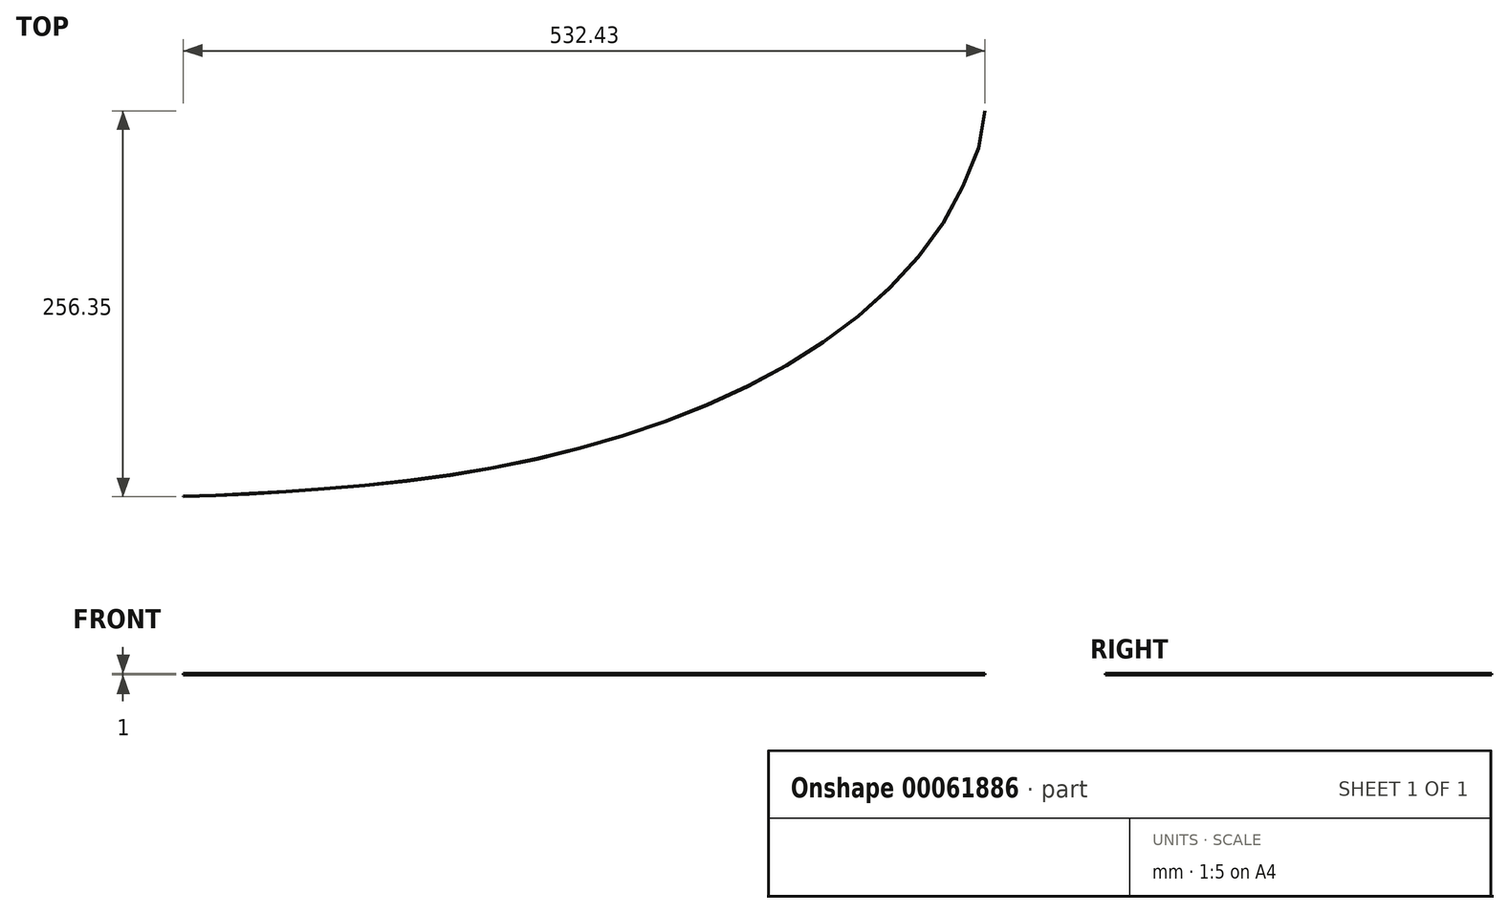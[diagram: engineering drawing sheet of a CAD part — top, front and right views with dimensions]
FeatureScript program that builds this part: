
annotation { "Feature Type Name" : "Feature", "Feature Type Description" : "" }
export const myFeature = defineFeature(function(context is Context, id is Id, definition is map)
    precondition{}
    {
        {
            var Q0;
            Q0=qCreatedBy(makeId("Top.planeOp"),FACE);
            var sketch = newSketch(context, id + "F0", { "sketchPlane" : qUnion([Q0])});
            skPoint(sketch, "E0", {"position": v(15.35, 547.94) * mm});
            skPoint(sketch, "E1", {"position": v(32.44, 548.38) * mm});
            skPoint(sketch, "E2", {"position": v(51.35, 549.15) * mm});
            skPoint(sketch, "E3", {"position": v(72.4, 550.32) * mm});
            skPoint(sketch, "E4", {"position": v(96.02, 551.9) * mm});
            skPoint(sketch, "E5", {"position": v(122.25, 553.98) * mm});
            skPoint(sketch, "E6", {"position": v(151.64, 556.75) * mm});
            skPoint(sketch, "E7", {"position": v(182.69, 560.56) * mm});
            skPoint(sketch, "E8", {"position": v(214.47, 565.65) * mm});
            skPoint(sketch, "E9", {"position": v(246.92, 572.1) * mm});
            skPoint(sketch, "E10", {"position": v(279.38, 580.02) * mm});
            skPoint(sketch, "E11", {"position": v(311.83, 589.54) * mm});
            skPoint(sketch, "E12", {"position": v(374.47, 613.63) * mm});
            skPoint(sketch, "E13", {"position": v(343.6, 600.72) * mm});
            skPoint(sketch, "E14", {"position": v(404.09, 628.3) * mm});
            skPoint(sketch, "E15", {"position": v(432, 644.78) * mm});
            skPoint(sketch, "E16", {"position": v(457.8, 663.1) * mm});
            skPoint(sketch, "E17", {"position": v(481.25, 683.18) * mm});
            skPoint(sketch, "E18", {"position": v(501.93, 705.07) * mm});
            skPoint(sketch, "E19", {"position": v(519.4, 728.72) * mm});
            skPoint(sketch, "E20", {"position": v(533.25, 754.2) * mm});
            skPoint(sketch, "E21", {"position": v(544.02, 781.68) * mm});
            skPoint(sketch, "E22", {"position": v(547.78, 803.84) * mm});
            skFitSpline(sketch, "E23", {"points": [v(15.35, 547.94) * mm, v(32.44, 548.38) * mm, v(51.35, 549.15) * mm, v(72.4, 550.32) * mm, v(96.02, 551.9) * mm, v(122.25, 553.98) * mm, v(151.64, 556.75) * mm, v(182.7, 560.56) * mm, v(214.47, 565.65) * mm, v(246.92, 572.1) * mm, v(279.38, 580.02) * mm, v(311.83, 589.54) * mm, v(343.6, 600.72) * mm, v(374.47, 613.63) * mm, v(404.1, 628.3) * mm, v(432, 644.78) * mm, v(457.8, 663.1) * mm, v(481.25, 683.18) * mm, v(501.93, 705.07) * mm, v(519.4, 728.72) * mm, v(533.25, 754.2) * mm, v(544.02, 781.68) * mm, v(547.78, 803.84) * mm], "startDerivative": vector(341.78, 8.55) * mm, "endDerivative": vector(18.26, 149.08) * mm});
            skPoint(sketch, "E24.0.1.0", {"position": v(15.35, 548.4) * mm});
            skPoint(sketch, "E24.0.1.1", {"position": v(19.35, 548.5) * mm});
            skPoint(sketch, "E24.0.1.2", {"position": v(32.44, 548.83) * mm});
            skPoint(sketch, "E24.0.1.3", {"position": v(51.35, 549.6) * mm});
            skPoint(sketch, "E24.0.1.4", {"position": v(72.4, 550.77) * mm});
            skPoint(sketch, "E24.0.1.5", {"position": v(96.02, 552.35) * mm});
            skPoint(sketch, "E24.0.1.6", {"position": v(122.25, 554.43) * mm});
            skPoint(sketch, "E24.0.1.7", {"position": v(151.64, 557.2) * mm});
            skPoint(sketch, "E24.0.1.8", {"position": v(182.7, 561) * mm});
            skPoint(sketch, "E24.0.1.9", {"position": v(214.47, 566.1) * mm});
            skPoint(sketch, "E24.0.1.10", {"position": v(246.92, 572.55) * mm});
            skPoint(sketch, "E24.0.1.11", {"position": v(279.38, 580.47) * mm});
            skPoint(sketch, "E24.0.1.12", {"position": v(311.83, 589.99) * mm});
            skPoint(sketch, "E24.0.1.13", {"position": v(343.6, 601.17) * mm});
            skPoint(sketch, "E24.0.1.14", {"position": v(374.47, 614.08) * mm});
            skPoint(sketch, "E24.0.1.15", {"position": v(404.1, 628.75) * mm});
            skPoint(sketch, "E24.0.1.16", {"position": v(432, 645.23) * mm});
            skPoint(sketch, "E24.0.1.17", {"position": v(457.8, 663.54) * mm});
            skPoint(sketch, "E24.0.1.18", {"position": v(481.25, 683.63) * mm});
            skPoint(sketch, "E24.0.1.19", {"position": v(501.93, 705.52) * mm});
            skPoint(sketch, "E24.0.1.20", {"position": v(519.4, 729.17) * mm});
            skPoint(sketch, "E24.0.1.21", {"position": v(533.25, 754.66) * mm});
            skPoint(sketch, "E24.0.1.22", {"position": v(544.02, 782.13) * mm});
            skPoint(sketch, "E24.0.1.23", {"position": v(547.53, 802.3) * mm});
            skPoint(sketch, "E24.0.1.24", {"position": v(547.78, 804.3) * mm});
            skLineSegment(sketch, "E24.direction1", {"start": v(15.35, 547.94) * mm, "end": v(40.35, 547.94) * mm, "construction": true});
            skLineSegment(sketch, "E24.direction2", {"start": v(15.35, 547.94) * mm, "end": v(15.35, 548.4) * mm, "construction": true});
            skFitSpline(sketch, "E25", {"points": [v(15.35, 548.4) * mm, v(32.44, 548.83) * mm, v(51.35, 549.6) * mm, v(72.4, 550.77) * mm, v(96.02, 552.35) * mm, v(122.25, 554.43) * mm, v(151.64, 557.2) * mm, v(182.7, 561) * mm, v(214.47, 566.1) * mm, v(246.92, 572.55) * mm, v(279.38, 580.47) * mm, v(311.83, 589.99) * mm, v(343.6, 601.17) * mm, v(374.47, 614.08) * mm, v(404.1, 628.75) * mm, v(432, 645.23) * mm, v(457.8, 663.54) * mm, v(481.25, 683.63) * mm, v(501.93, 705.52) * mm, v(519.4, 729.17) * mm, v(533.25, 754.66) * mm, v(544.02, 782.13) * mm, v(547.78, 804.3) * mm], "startDerivative": vector(341.78, 8.55) * mm, "endDerivative": vector(18.26, 149.08) * mm});
            skLineSegment(sketch, "E26", {"start": v(15.35, 548.4) * mm, "end": v(15.35, 547.94) * mm});
            skLineSegment(sketch, "E27", {"start": v(547.78, 804.3) * mm, "end": v(547.78, 803.84) * mm});
            skSolve(sketch);
        }
        {
            var Q0;
            Q0 = qSketchRegion(id + "F0", true);
            var Q1;
            Q1=sQuery(id+"F0.wireOp",EDGE,"E23");
            extrude(context, id + "F1", {"entities" : qUnion([Q0]), "surfaceEntities" : qUnion([Q1]), "endBound" : BoundingType.SYMMETRIC, "depth" : 1 * mm});
        }
    });
